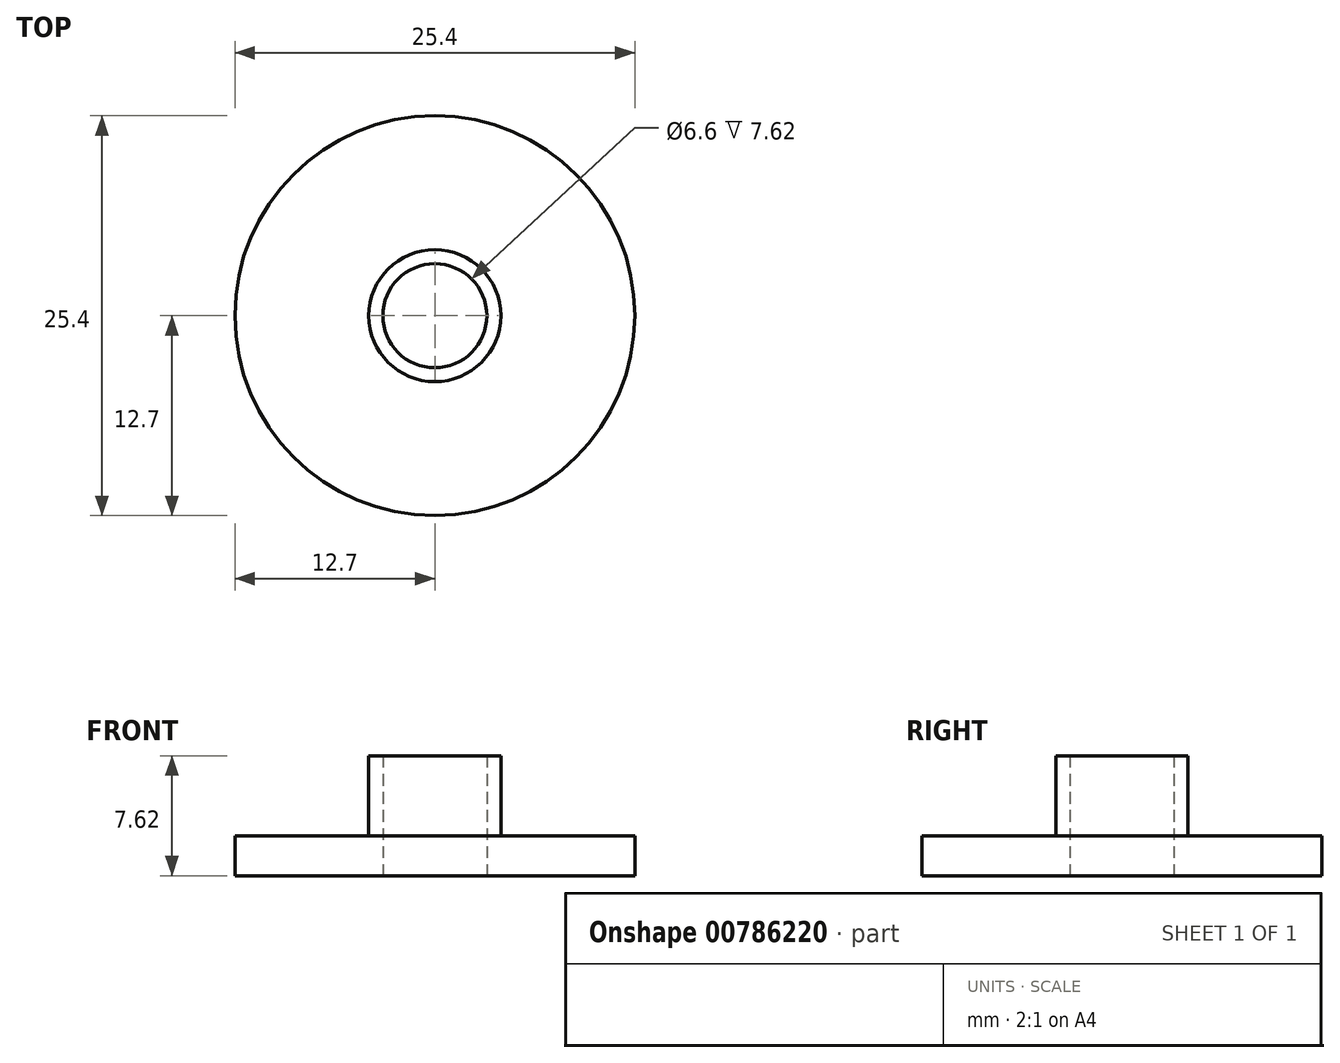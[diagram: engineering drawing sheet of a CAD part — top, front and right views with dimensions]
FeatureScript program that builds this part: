
annotation { "Feature Type Name" : "Feature", "Feature Type Description" : "" }
export const myFeature = defineFeature(function(context is Context, id is Id, definition is map)
    precondition{}
    {
        {
            var Q0;
            Q0=qCreatedBy(makeId("Top.planeOp"),FACE);
            var sketch = newSketch(context, id + "F0", { "sketchPlane" : qUnion([Q0])});
            skCircle(sketch, "E0", {"center": v(0, 0) * mm, "radius": 12.7 * mm});
            skSolve(sketch);
        }
        {
            var Q0;
            Q0=qSketchRegion(id+"F0",true);
            extrude(context, id + "F1", {"entities" : qUnion([Q0]), "depth" : 2.54 * mm, "offsetDistance" : 25.4 * mm});
        }
        {
            var Q0;
            Q0=qCreatedBy(makeId("Top.planeOp"),FACE);
            var sketch = newSketch(context, id + "F2", { "sketchPlane" : qUnion([Q0])});
            skCircle(sketch, "E1", {"center": v(0, 0) * mm, "radius": 4.2 * mm});
            skSolve(sketch);
        }
        {
            var Q0;
            Q0=qSketchRegion(id+"F2",true);
            extrude(context, id + "F3", {"entities" : qUnion([Q0]), "operationType" : NewBodyOperationType.ADD, "depth" : 7.62 * mm, "offsetDistance" : 25.4 * mm});
        }
        {
            var Q0;
            Q0=qCreatedBy(makeId("Top.planeOp"),FACE);
            var sketch = newSketch(context, id + "F4", { "sketchPlane" : qUnion([Q0])});
            skCircle(sketch, "E2", {"center": v(0, 0) * mm, "radius": 3.3 * mm});
            skSolve(sketch);
        }
        {
            var Q0;
            Q0=qSketchRegion(id+"F4",true);
            extrude(context, id + "F5", {"entities" : qUnion([Q0]), "operationType" : NewBodyOperationType.REMOVE, "endBound" : BoundingType.THROUGH_ALL, "depth" : 25.4 * mm, "offsetDistance" : 25.4 * mm});
        }
    });
